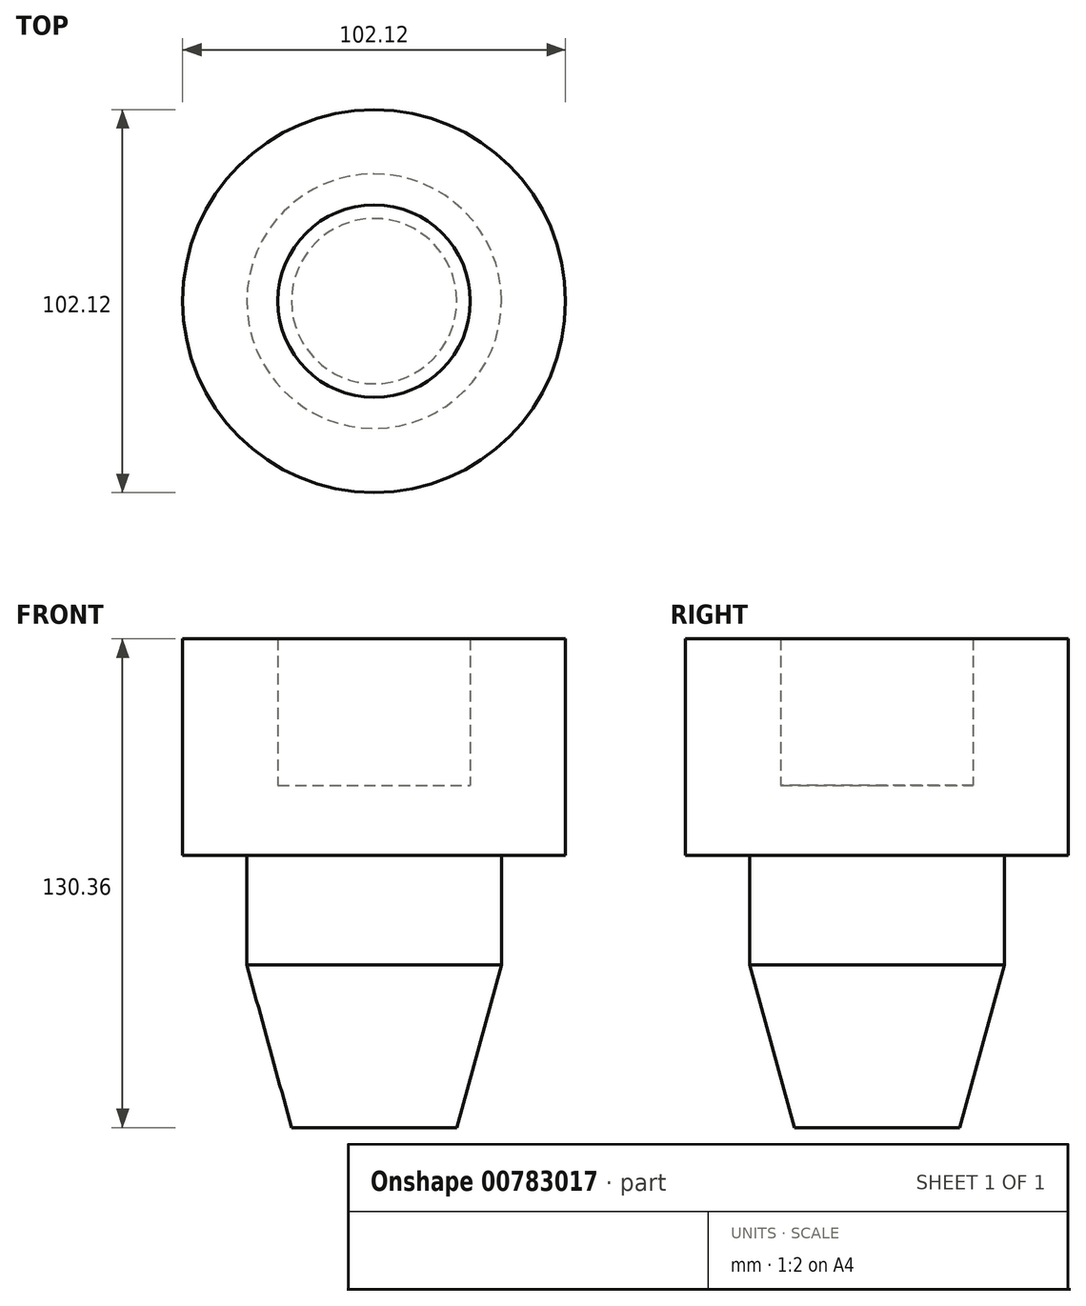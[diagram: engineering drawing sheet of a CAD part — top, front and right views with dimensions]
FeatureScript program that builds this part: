
annotation { "Feature Type Name" : "Feature", "Feature Type Description" : "" }
export const myFeature = defineFeature(function(context is Context, id is Id, definition is map)
    precondition{}
    {
        {
            var Q0;
            Q0=qCreatedBy(makeId("Front.planeOp"),FACE);
            var sketch = newSketch(context, id + "F0", { "sketchPlane" : qUnion([Q0])});
            skLineSegment(sketch, "E0", {"start": v(0, 0) * mm, "end": v(0, 91.28) * mm});
            skLineSegment(sketch, "E1", {"start": v(0, 91.28) * mm, "end": v(-25.66, 91.28) * mm});
            skLineSegment(sketch, "E2", {"start": v(-25.66, 91.28) * mm, "end": v(-25.66, 130.36) * mm});
            skLineSegment(sketch, "E3", {"start": v(-25.66, 130.36) * mm, "end": v(-51.06, 130.36) * mm});
            skLineSegment(sketch, "E4", {"start": v(-51.06, 130.36) * mm, "end": v(-51.06, 72.54) * mm});
            skLineSegment(sketch, "E5", {"start": v(-51.06, 72.54) * mm, "end": v(-33.95, 72.54) * mm});
            skLineSegment(sketch, "E6", {"start": v(-33.95, 72.54) * mm, "end": v(-33.95, 43.33) * mm});
            skLineSegment(sketch, "E7", {"start": v(-33.95, 43.33) * mm, "end": v(-22.03, 0) * mm});
            skLineSegment(sketch, "E8", {"start": v(-22.03, 0) * mm, "end": v(0, 0) * mm});
            skSolve(sketch);
        }
        {
            var Q0;
            Q0=makeQuery(id+"F0.imprint","IMPRINT",FACE,{"disambiguationData":[TD([[makeQuery(id+"F0.imprint","IMPRINT",EDGE,{"derivedFrom":sQuery(id+"F0.wireOp",EDGE,"E0")}),1.0]])]});
            var Q1;
            Q1=sQuery(id+"F0.wireOp",EDGE,"E0");
            revolve(context, id + "F1", {"surfaceOperationType" : NewSurfaceOperationType.NEW, "entities" : qUnion([Q0]), "axis" : qUnion([Q1]), "revolveType" : RevolveType.FULL});
        }
    });
